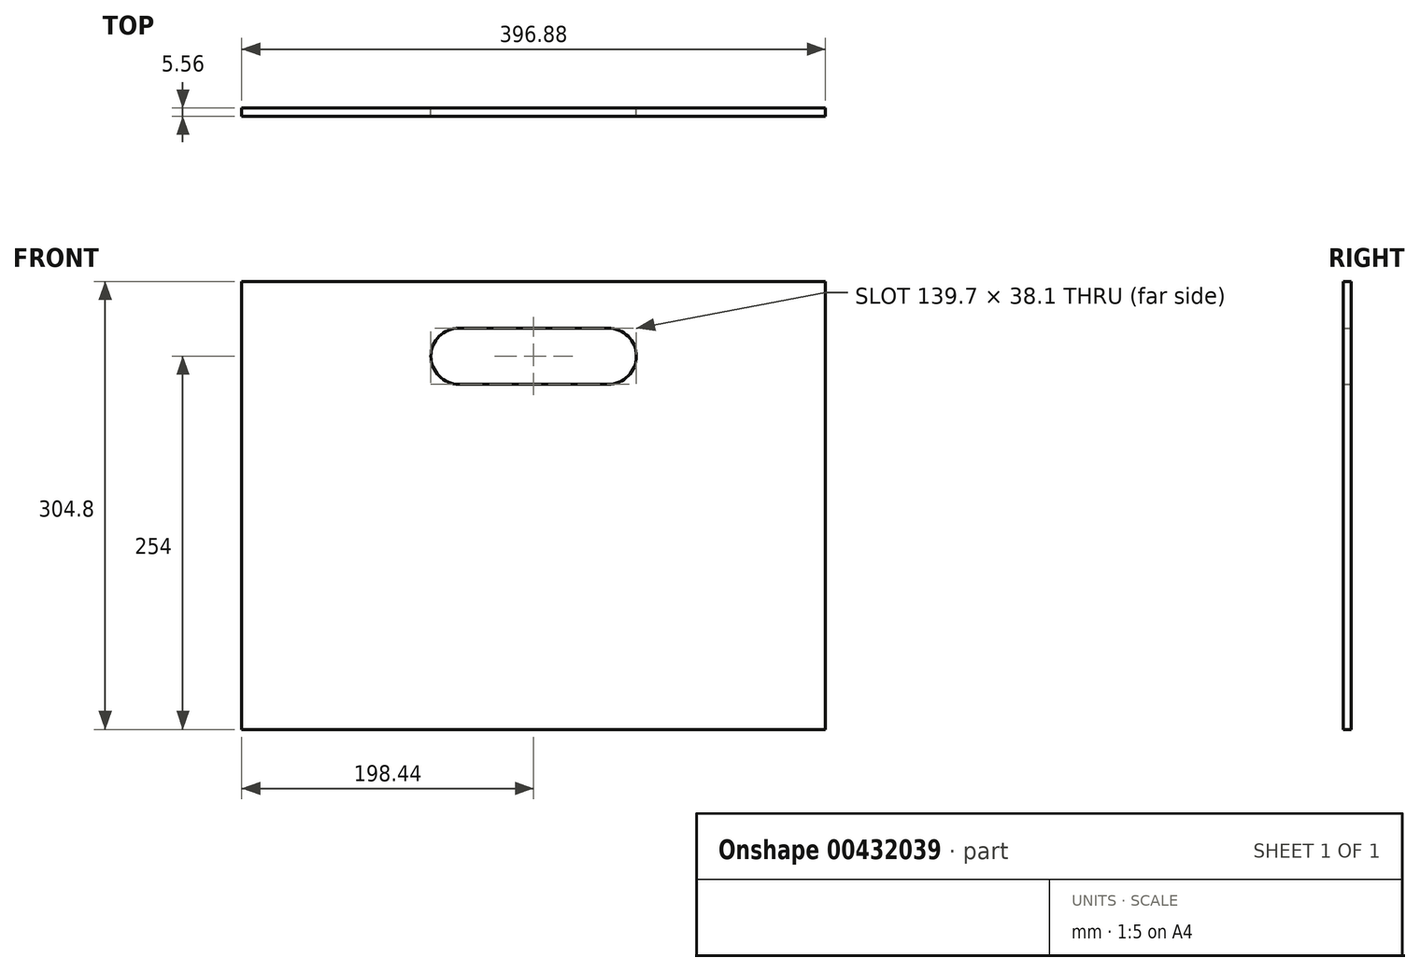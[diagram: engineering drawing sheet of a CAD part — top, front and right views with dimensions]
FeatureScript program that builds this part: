
annotation { "Feature Type Name" : "Feature", "Feature Type Description" : "" }
export const myFeature = defineFeature(function(context is Context, id is Id, definition is map)
    precondition{}
    {
        {
            var Q0;
            Q0=qCreatedBy(makeId("Front.planeOp"),FACE);
            var sketch = newSketch(context, id + "F0", { "sketchPlane" : qUnion([Q0])});
            skLineSegment(sketch, "E0", {"start": v(0, 0) * mm, "end": v(0, 6.35) * mm, "construction": true});
            skLineSegment(sketch, "E1", {"start": v(0, 6.35) * mm, "end": v(0, 158.75) * mm, "construction": true});
            skLineSegment(sketch, "E2.bottom", {"start": v(-198.44, 6.35) * mm, "end": v(198.44, 6.35) * mm});
            skLineSegment(sketch, "E2.top", {"start": v(-198.44, 311.15) * mm, "end": v(198.44, 311.15) * mm});
            skLineSegment(sketch, "E2.left", {"start": v(-198.44, 6.35) * mm, "end": v(-198.44, 311.15) * mm});
            skLineSegment(sketch, "E2.right", {"start": v(198.44, 6.35) * mm, "end": v(198.44, 311.15) * mm});
            skPoint(sketch, "E2.middle", {"position": v(0, 158.75) * mm});
            skLineSegment(sketch, "E3", {"start": v(0, 311.15) * mm, "end": v(0, 260.35) * mm, "construction": true});
            skPoint(sketch, "E3.endSnap0", {"position": v(0, 311.15) * mm});
            skLineSegment(sketch, "E4", {"start": v(0, 260.35) * mm, "end": v(-50.8, 260.35) * mm, "construction": true});
            skLineSegment(sketch, "E5.MirrorCS", {"start": v(0, 260.35) * mm, "end": v(50.8, 260.35) * mm, "construction": true});
            skCircle(sketch, "E6", {"center": v(-50.8, 260.35) * mm, "radius": 19.05 * mm});
            skCircle(sketch, "E7.MirrorC", {"center": v(50.8, 260.35) * mm, "radius": 19.05 * mm});
            skLineSegment(sketch, "E8", {"start": v(50.8, 260.35) * mm, "end": v(50.8, 279.4) * mm, "construction": true});
            skLineSegment(sketch, "E9", {"start": v(-50.8, 260.35) * mm, "end": v(-50.8, 279.4) * mm, "construction": true});
            skLineSegment(sketch, "E10", {"start": v(-50.8, 279.4) * mm, "end": v(50.8, 279.4) * mm});
            skLineSegment(sketch, "E11.MirrorCS", {"start": v(-50.8, 241.3) * mm, "end": v(50.8, 241.3) * mm});
            skSolve(sketch);
        }
        {
            var Q0;
            Q0=makeQuery(id+"F0.imprint","IMPRINT",FACE,{"disambiguationData":[TD([[makeQuery(id+"F0.imprint","IMPRINT",EDGE,{"derivedFrom":sQuery(id+"F0.wireOp",EDGE,"E2.bottom")}),1.0]])]});
            extrude(context, id + "F1", {"entities" : qUnion([Q0]), "depth" : 5.56 * mm});
        }
    });
